# Revit family: Festpunktkonsole  50- 38
name_source: partatom
category: HLS-Bauteile
revit_build: Autodesk Revit 2017 (Build: 20190507_1515(x64)
units: mm (PartAtom-declared; Revit-internal decimal feet)

## family parameters
Basisbauteil = Fläche
Beim Laden mit Abzugskörper schneiden = Nein
Bemaßung runder Anschluss = Durchmesser verwenden
Gemeinsam genutzt = Ja
Raumberechnungspunkt = Nein
Teiletyp = Normal

## types (7) — shared parameters
Artikelnummer = 9997799
Breite Platte = 200 mm  [stored 0.656168 ft]
Breite Profil = 50 mm  [stored 0.164042 ft]
EAN = 4250928446947
Fabrikat = MEFA
Firma = MEFA Befestigungs- und Montagesysteme GmbH
Gewicht = 7.40 kg
Gewicht pro Bauteil = 7.40 kg
Höhe Profil = 38 mm
Kurztext1 = Festpunktkonsole U-Profil 50/38
Kurztext2 = L= 750 mm Platte blank
Langloch Platte = 14x27 mm
Lochabstand = 150 mm
Lochdurchmesser = 14 mm
Länge Konsole = 750 mm
Länge Platte = 200 mm  [stored 0.656168 ft]
Material = Stahl
Materialname C-Profil = S235JR
Materialname Platte = S235JR
Oberflaeche = blank
Profil = U-Profil
S = 10 mm  [stored 0.0328084 ft]
Stärke Platte = 10 mm  [stored 0.0328084 ft]
Vorgabe-Ansicht = 1219 mm
für Rohrdurchmesser = ab 20 mm
max. zul. Last F1 = 0.00 kip
max. zul. Last F2 = 0.00 kip
max. zul. Last q0 = 0.000 kip/ft
zero-valued in all types: Stärke Profil

## per-type parameters (varying)
| type | Länge U Stahl |
| Festpunktkonsole  50/38, L=100 | U-Stahl 50-38-100 bis 700 : U-Stahl 50-38 L=100mm |
| Festpunktkonsole  50/38, L=200 | U-Stahl 50-38-100 bis 700 : U-Stahl 50-38 L=200mm |
| Festpunktkonsole  50/38, L=300 | U-Stahl 50-38-100 bis 700 : U-Stahl 50-38 L=300mm |
| Festpunktkonsole  50/38, L=400 | U-Stahl 50-38-100 bis 700 : U-Stahl 50-38 L=400mm |
| Festpunktkonsole  50/38, L=500 | U-Stahl 50-38-100 bis 700 : U-Stahl 50-38 L=500mm |
| Festpunktkonsole  50/38, L=600 | U-Stahl 50-38-100 bis 700 : U-Stahl 50-38 L=600mm |
| Festpunktkonsole  50/38, L=700 | U-Stahl 50-38-100 bis 700 : U-Stahl 50-38 L=700mm |

note: [stored X ft] marks values corroborated as IEEE doubles in the binary element streams (Revit-internal decimal feet)
